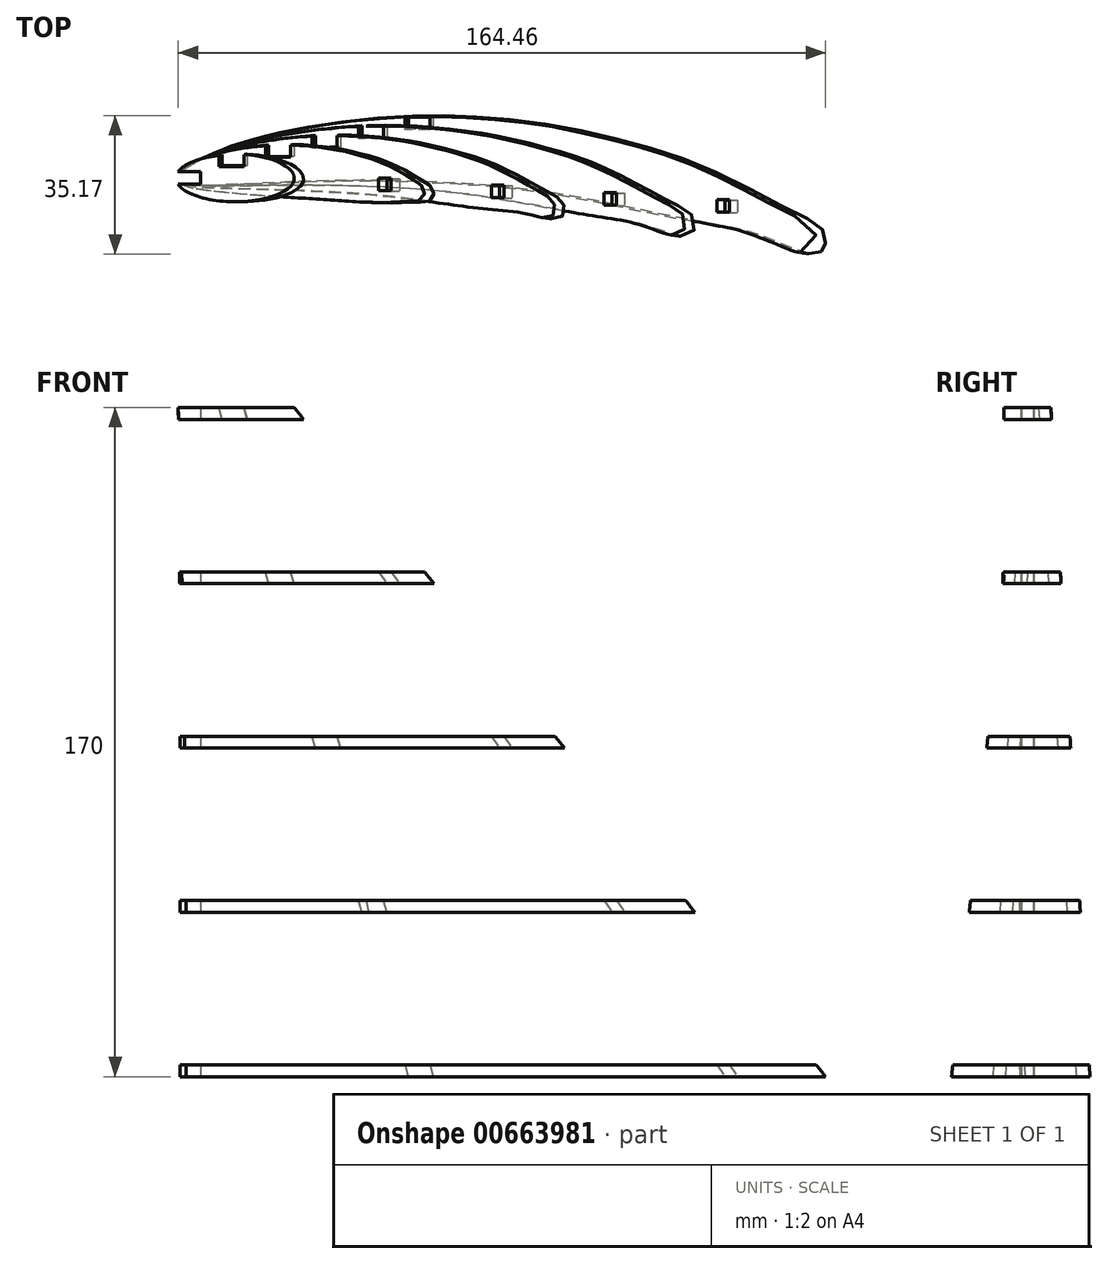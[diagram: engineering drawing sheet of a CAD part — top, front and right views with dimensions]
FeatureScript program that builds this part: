
annotation { "Feature Type Name" : "Feature", "Feature Type Description" : "" }
export const myFeature = defineFeature(function(context is Context, id is Id, definition is map)
    precondition{}
    {
        {
            var Q0;
            Q0=qCreatedBy(makeId("Top.planeOp"),FACE);
            var sketch = newSketch(context, id + "F0", { "sketchPlane" : qUnion([Q0])});
            skLineSegment(sketch, "E0", {"start": v(1, 1.71) * mm, "end": v(3.22, 2.99) * mm});
            skLineSegment(sketch, "E1", {"start": v(3.22, 2.99) * mm, "end": v(5.44, 4.24) * mm});
            skLineSegment(sketch, "E2", {"start": v(5.44, 4.24) * mm, "end": v(7.68, 5.43) * mm});
            skLineSegment(sketch, "E3", {"start": v(7.68, 5.43) * mm, "end": v(9.99, 6.53) * mm});
            skLineSegment(sketch, "E4", {"start": v(9.99, 6.53) * mm, "end": v(12.3, 7.5) * mm});
            skLineSegment(sketch, "E5", {"start": v(12.3, 7.5) * mm, "end": v(14.68, 8.38) * mm});
            skLineSegment(sketch, "E6", {"start": v(14.68, 8.38) * mm, "end": v(17.1, 9.17) * mm});
            skLineSegment(sketch, "E7", {"start": v(17.1, 9.17) * mm, "end": v(19.55, 9.87) * mm});
            skLineSegment(sketch, "E8", {"start": v(19.55, 9.87) * mm, "end": v(22.03, 10.5) * mm});
            skLineSegment(sketch, "E9", {"start": v(22.03, 10.5) * mm, "end": v(26.45, 11.52) * mm});
            skLineSegment(sketch, "E10", {"start": v(26.45, 11.52) * mm, "end": v(29.5, 12.16) * mm});
            skLineSegment(sketch, "E11", {"start": v(29.5, 12.16) * mm, "end": v(34.51, 13.11) * mm});
            skLineSegment(sketch, "E12", {"start": v(34.51, 13.11) * mm, "end": v(37.02, 13.54) * mm});
            skLineSegment(sketch, "E13", {"start": v(37.02, 13.54) * mm, "end": v(39.53, 13.94) * mm});
            skLineSegment(sketch, "E14", {"start": v(39.53, 13.94) * mm, "end": v(42.04, 14.3) * mm});
            skLineSegment(sketch, "E15", {"start": v(42.04, 14.3) * mm, "end": v(44.56, 14.62) * mm});
            skLineSegment(sketch, "E16", {"start": v(44.56, 14.62) * mm, "end": v(48.06, 15.01) * mm});
            skLineSegment(sketch, "E17", {"start": v(48.06, 15.01) * mm, "end": v(49.61, 15.16) * mm});
            skLineSegment(sketch, "E18", {"start": v(49.61, 15.16) * mm, "end": v(52.14, 15.37) * mm});
            skLineSegment(sketch, "E19", {"start": v(52.14, 15.37) * mm, "end": v(54.68, 15.53) * mm});
            skLineSegment(sketch, "E20", {"start": v(54.68, 15.53) * mm, "end": v(57.22, 15.66) * mm});
            skLineSegment(sketch, "E21", {"start": v(57.22, 15.66) * mm, "end": v(59.76, 15.76) * mm});
            skLineSegment(sketch, "E22", {"start": v(59.76, 15.76) * mm, "end": v(62.3, 15.81) * mm});
            skLineSegment(sketch, "E23", {"start": v(62.3, 15.81) * mm, "end": v(64.85, 15.83) * mm});
            skLineSegment(sketch, "E24", {"start": v(64.85, 15.83) * mm, "end": v(67.4, 15.82) * mm});
            skLineSegment(sketch, "E25", {"start": v(67.4, 15.82) * mm, "end": v(69.95, 15.77) * mm});
            skLineSegment(sketch, "E26", {"start": v(69.95, 15.77) * mm, "end": v(72.67, 15.68) * mm});
            skLineSegment(sketch, "E27", {"start": v(72.67, 15.68) * mm, "end": v(75.03, 15.57) * mm});
            skLineSegment(sketch, "E28", {"start": v(75.03, 15.57) * mm, "end": v(77.57, 15.42) * mm});
            skLineSegment(sketch, "E29", {"start": v(77.57, 15.42) * mm, "end": v(80.11, 15.23) * mm});
            skLineSegment(sketch, "E30", {"start": v(80.11, 15.23) * mm, "end": v(82.65, 15.02) * mm});
            skLineSegment(sketch, "E31", {"start": v(82.65, 15.02) * mm, "end": v(85.18, 14.77) * mm});
            skLineSegment(sketch, "E32", {"start": v(85.18, 14.77) * mm, "end": v(87.7, 14.49) * mm});
            skLineSegment(sketch, "E33", {"start": v(87.7, 14.49) * mm, "end": v(90.23, 14.17) * mm});
            skLineSegment(sketch, "E34", {"start": v(90.23, 14.17) * mm, "end": v(92.75, 13.82) * mm});
            skLineSegment(sketch, "E35", {"start": v(92.75, 13.82) * mm, "end": v(95.26, 13.44) * mm});
            skLineSegment(sketch, "E36", {"start": v(95.26, 13.44) * mm, "end": v(97.77, 13.02) * mm});
            skLineSegment(sketch, "E37", {"start": v(97.77, 13.02) * mm, "end": v(100.27, 12.56) * mm});
            skLineSegment(sketch, "E38", {"start": v(100.27, 12.56) * mm, "end": v(102.77, 12.08) * mm});
            skLineSegment(sketch, "E39", {"start": v(102.77, 12.08) * mm, "end": v(105.26, 11.56) * mm});
            skLineSegment(sketch, "E40", {"start": v(105.26, 11.56) * mm, "end": v(107.74, 11) * mm});
            skLineSegment(sketch, "E41", {"start": v(107.74, 11) * mm, "end": v(110.22, 10.41) * mm});
            skLineSegment(sketch, "E42", {"start": v(110.22, 10.41) * mm, "end": v(112.68, 9.79) * mm});
            skLineSegment(sketch, "E43", {"start": v(112.68, 9.79) * mm, "end": v(115.14, 9.13) * mm});
            skLineSegment(sketch, "E44", {"start": v(115.14, 9.13) * mm, "end": v(117.6, 8.44) * mm});
            skLineSegment(sketch, "E45", {"start": v(117.6, 8.44) * mm, "end": v(120.03, 7.72) * mm});
            skLineSegment(sketch, "E46", {"start": v(120.03, 7.72) * mm, "end": v(121.72, 7.2) * mm});
            skLineSegment(sketch, "E47", {"start": v(121.72, 7.2) * mm, "end": v(124.88, 6.17) * mm});
            skLineSegment(sketch, "E48", {"start": v(124.88, 6.17) * mm, "end": v(127.29, 5.34) * mm});
            skLineSegment(sketch, "E49", {"start": v(127.29, 5.34) * mm, "end": v(129.68, 4.48) * mm});
            skLineSegment(sketch, "E50", {"start": v(129.68, 4.48) * mm, "end": v(132.06, 3.58) * mm});
            skLineSegment(sketch, "E51", {"start": v(132.06, 3.58) * mm, "end": v(134.43, 2.64) * mm});
            skLineSegment(sketch, "E52", {"start": v(134.43, 2.64) * mm, "end": v(136.78, 1.66) * mm});
            skLineSegment(sketch, "E53", {"start": v(136.78, 1.66) * mm, "end": v(139.1, 0.64) * mm});
            skLineSegment(sketch, "E54", {"start": v(139.1, 0.64) * mm, "end": v(142.17, -0.78) * mm});
            skLineSegment(sketch, "E55", {"start": v(142.17, -0.78) * mm, "end": v(143.7, -1.53) * mm});
            skLineSegment(sketch, "E56", {"start": v(143.7, -1.53) * mm, "end": v(145.97, -2.68) * mm});
            skLineSegment(sketch, "E57", {"start": v(145.97, -2.68) * mm, "end": v(148.22, -3.85) * mm});
            skLineSegment(sketch, "E58", {"start": v(148.22, -3.85) * mm, "end": v(152.69, -6.28) * mm});
            skLineSegment(sketch, "E59", {"start": v(152.69, -6.28) * mm, "end": v(157.13, -8.76) * mm});
            skLineSegment(sketch, "E60", {"start": v(1, 1.71) * mm, "end": v(0.87, 1.54) * mm});
            skLineSegment(sketch, "E61", {"start": v(0.87, 1.54) * mm, "end": v(0.73, 1.38) * mm});
            skLineSegment(sketch, "E62", {"start": v(0.73, 1.38) * mm, "end": v(0.6, 1.21) * mm});
            skLineSegment(sketch, "E63", {"start": v(0.6, 1.21) * mm, "end": v(0.48, 1.05) * mm});
            skLineSegment(sketch, "E64", {"start": v(0.48, 1.05) * mm, "end": v(0.42, 0.97) * mm});
            skLineSegment(sketch, "E65", {"start": v(0.42, 0.97) * mm, "end": v(0.37, 0.9) * mm});
            skLineSegment(sketch, "E66", {"start": v(0.37, 0.9) * mm, "end": v(0.33, 0.84) * mm});
            skLineSegment(sketch, "E67", {"start": v(0.33, 0.84) * mm, "end": v(0.27, 0.74) * mm});
            skLineSegment(sketch, "E68", {"start": v(0.27, 0.74) * mm, "end": v(0.23, 0.67) * mm});
            skLineSegment(sketch, "E69", {"start": v(0.23, 0.67) * mm, "end": v(0.19, 0.6) * mm});
            skLineSegment(sketch, "E70", {"start": v(0.19, 0.6) * mm, "end": v(0.15, 0.52) * mm});
            skLineSegment(sketch, "E71", {"start": v(0.15, 0.52) * mm, "end": v(0.12, 0.45) * mm});
            skLineSegment(sketch, "E72", {"start": v(0.12, 0.45) * mm, "end": v(0.1, 0.38) * mm});
            skLineSegment(sketch, "E73", {"start": v(0.1, 0.38) * mm, "end": v(0.07, 0.32) * mm});
            skLineSegment(sketch, "E74", {"start": v(0.07, 0.32) * mm, "end": v(0.05, 0.25) * mm});
            skLineSegment(sketch, "E75", {"start": v(0.05, 0.25) * mm, "end": v(0.03, 0.19) * mm});
            skLineSegment(sketch, "E76", {"start": v(0.03, 0.19) * mm, "end": v(0.02, 0.12) * mm});
            skLineSegment(sketch, "E77", {"start": v(0.02, 0.12) * mm, "end": v(0, 0.06) * mm});
            skLineSegment(sketch, "E78", {"start": v(0, 0.06) * mm, "end": v(0, 0) * mm});
            skLineSegment(sketch, "E79", {"start": v(0, 0) * mm, "end": v(0, -0.06) * mm});
            skLineSegment(sketch, "E80", {"start": v(0, -0.06) * mm, "end": v(0, -0.12) * mm});
            skLineSegment(sketch, "E81", {"start": v(0, -0.12) * mm, "end": v(0, -0.18) * mm});
            skLineSegment(sketch, "E82", {"start": v(0, -0.18) * mm, "end": v(0, -0.23) * mm});
            skLineSegment(sketch, "E83", {"start": v(0, -0.23) * mm, "end": v(0.02, -0.29) * mm});
            skLineSegment(sketch, "E84", {"start": v(0.02, -0.29) * mm, "end": v(0.03, -0.34) * mm});
            skLineSegment(sketch, "E85", {"start": v(0.03, -0.34) * mm, "end": v(0.05, -0.4) * mm});
            skLineSegment(sketch, "E86", {"start": v(0.05, -0.4) * mm, "end": v(0.07, -0.44) * mm});
            skLineSegment(sketch, "E87", {"start": v(0.07, -0.44) * mm, "end": v(0.1, -0.5) * mm});
            skLineSegment(sketch, "E88", {"start": v(0.1, -0.5) * mm, "end": v(0.12, -0.54) * mm});
            skLineSegment(sketch, "E89", {"start": v(0.12, -0.54) * mm, "end": v(0.15, -0.6) * mm});
            skLineSegment(sketch, "E90", {"start": v(0.15, -0.6) * mm, "end": v(0.18, -0.64) * mm});
            skLineSegment(sketch, "E91", {"start": v(0.18, -0.64) * mm, "end": v(0.22, -0.68) * mm});
            skLineSegment(sketch, "E92", {"start": v(0.22, -0.68) * mm, "end": v(0.25, -0.73) * mm});
            skLineSegment(sketch, "E93", {"start": v(0.25, -0.73) * mm, "end": v(0.3, -0.77) * mm});
            skLineSegment(sketch, "E94", {"start": v(0.3, -0.77) * mm, "end": v(0.34, -0.81) * mm});
            skLineSegment(sketch, "E95", {"start": v(0.34, -0.81) * mm, "end": v(0.39, -0.86) * mm});
            skLineSegment(sketch, "E96", {"start": v(0.39, -0.86) * mm, "end": v(0.44, -0.9) * mm});
            skLineSegment(sketch, "E97", {"start": v(0.44, -0.9) * mm, "end": v(0.5, -0.94) * mm});
            skLineSegment(sketch, "E98", {"start": v(0.5, -0.94) * mm, "end": v(0.6, -1.01) * mm});
            skLineSegment(sketch, "E99", {"start": v(0.6, -1.01) * mm, "end": v(0.73, -1.08) * mm});
            skLineSegment(sketch, "E100", {"start": v(0.73, -1.08) * mm, "end": v(0.87, -1.15) * mm});
            skLineSegment(sketch, "E101", {"start": v(0.87, -1.15) * mm, "end": v(1.02, -1.22) * mm});
            skLineSegment(sketch, "E102", {"start": v(1.02, -1.22) * mm, "end": v(1.17, -1.28) * mm});
            skLineSegment(sketch, "E103", {"start": v(1.17, -1.28) * mm, "end": v(1.34, -1.33) * mm});
            skLineSegment(sketch, "E104", {"start": v(1.34, -1.33) * mm, "end": v(1.52, -1.39) * mm});
            skLineSegment(sketch, "E105", {"start": v(1.52, -1.39) * mm, "end": v(1.7, -1.44) * mm});
            skLineSegment(sketch, "E106", {"start": v(1.7, -1.44) * mm, "end": v(1.9, -1.48) * mm});
            skLineSegment(sketch, "E107", {"start": v(1.9, -1.48) * mm, "end": v(2.1, -1.53) * mm});
            skLineSegment(sketch, "E108", {"start": v(2.1, -1.53) * mm, "end": v(2.32, -1.57) * mm});
            skLineSegment(sketch, "E109", {"start": v(2.32, -1.57) * mm, "end": v(2.54, -1.6) * mm});
            skLineSegment(sketch, "E110", {"start": v(2.54, -1.6) * mm, "end": v(2.77, -1.64) * mm});
            skLineSegment(sketch, "E111", {"start": v(2.77, -1.64) * mm, "end": v(3, -1.67) * mm});
            skLineSegment(sketch, "E112", {"start": v(3, -1.67) * mm, "end": v(3.25, -1.7) * mm});
            skLineSegment(sketch, "E113", {"start": v(3.25, -1.7) * mm, "end": v(3.5, -1.73) * mm});
            skLineSegment(sketch, "E114", {"start": v(3.5, -1.73) * mm, "end": v(3.77, -1.75) * mm});
            skLineSegment(sketch, "E115", {"start": v(3.77, -1.75) * mm, "end": v(4.03, -1.77) * mm});
            skLineSegment(sketch, "E116", {"start": v(4.03, -1.77) * mm, "end": v(4.3, -1.8) * mm});
            skLineSegment(sketch, "E117", {"start": v(4.3, -1.8) * mm, "end": v(4.59, -1.8) * mm});
            skLineSegment(sketch, "E118", {"start": v(4.59, -1.8) * mm, "end": v(4.87, -1.82) * mm});
            skLineSegment(sketch, "E119", {"start": v(4.87, -1.82) * mm, "end": v(5.16, -1.83) * mm});
            skLineSegment(sketch, "E120", {"start": v(5.16, -1.83) * mm, "end": v(5.46, -1.84) * mm});
            skLineSegment(sketch, "E121", {"start": v(5.46, -1.84) * mm, "end": v(5.76, -1.85) * mm});
            skLineSegment(sketch, "E122", {"start": v(5.76, -1.85) * mm, "end": v(6.07, -1.86) * mm});
            skLineSegment(sketch, "E123", {"start": v(6.07, -1.86) * mm, "end": v(6.38, -1.86) * mm});
            skLineSegment(sketch, "E124", {"start": v(6.38, -1.86) * mm, "end": v(6.7, -1.87) * mm});
            skLineSegment(sketch, "E125", {"start": v(6.7, -1.87) * mm, "end": v(7.02, -1.87) * mm});
            skLineSegment(sketch, "E126", {"start": v(7.02, -1.87) * mm, "end": v(7.34, -1.87) * mm});
            skLineSegment(sketch, "E127", {"start": v(7.34, -1.87) * mm, "end": v(7.67, -1.87) * mm});
            skLineSegment(sketch, "E128", {"start": v(7.67, -1.87) * mm, "end": v(8, -1.87) * mm});
            skLineSegment(sketch, "E129", {"start": v(8, -1.87) * mm, "end": v(8.34, -1.86) * mm});
            skLineSegment(sketch, "E130", {"start": v(8.34, -1.86) * mm, "end": v(8.67, -1.86) * mm});
            skLineSegment(sketch, "E131", {"start": v(8.67, -1.86) * mm, "end": v(9.36, -1.85) * mm});
            skLineSegment(sketch, "E132", {"start": v(9.36, -1.85) * mm, "end": v(10.05, -1.83) * mm});
            skLineSegment(sketch, "E133", {"start": v(10.05, -1.83) * mm, "end": v(10.74, -1.82) * mm});
            skLineSegment(sketch, "E134", {"start": v(10.74, -1.82) * mm, "end": v(12.15, -1.78) * mm});
            skLineSegment(sketch, "E135", {"start": v(157.13, -8.76) * mm, "end": v(159.65, -9.9) * mm});
            skLineSegment(sketch, "E136", {"start": v(159.65, -9.9) * mm, "end": v(162.12, -11.02) * mm});
            skLineSegment(sketch, "E137", {"start": v(162.12, -11.02) * mm, "end": v(163.97, -12.8) * mm});
            skLineSegment(sketch, "E138", {"start": v(163.97, -12.8) * mm, "end": v(165.18, -13.97) * mm});
            skLineSegment(sketch, "E139", {"start": v(165.18, -13.97) * mm, "end": v(165.11, -15.41) * mm});
            skLineSegment(sketch, "E140", {"start": v(165.11, -15.41) * mm, "end": v(164.85, -16.72) * mm});
            skLineSegment(sketch, "E141", {"start": v(164.85, -16.72) * mm, "end": v(164.68, -17.32) * mm});
            skLineSegment(sketch, "E142", {"start": v(164.68, -17.32) * mm, "end": v(164.48, -17.86) * mm});
            skLineSegment(sketch, "E143", {"start": v(164.48, -17.86) * mm, "end": v(164.28, -18.24) * mm});
            skLineSegment(sketch, "E144", {"start": v(164.28, -18.24) * mm, "end": v(163.92, -18.7) * mm});
            skLineSegment(sketch, "E145", {"start": v(163.92, -18.7) * mm, "end": v(163.55, -18.98) * mm});
            skLineSegment(sketch, "E146", {"start": v(163.55, -18.98) * mm, "end": v(163.13, -19.18) * mm});
            skLineSegment(sketch, "E147", {"start": v(163.13, -19.18) * mm, "end": v(162.66, -19.3) * mm});
            skLineSegment(sketch, "E148", {"start": v(162.66, -19.3) * mm, "end": v(162.15, -19.36) * mm});
            skLineSegment(sketch, "E149", {"start": v(162.15, -19.36) * mm, "end": v(161.6, -19.35) * mm});
            skLineSegment(sketch, "E150", {"start": v(161.6, -19.35) * mm, "end": v(161, -19.28) * mm});
            skLineSegment(sketch, "E151", {"start": v(161, -19.28) * mm, "end": v(160.39, -19.16) * mm});
            skLineSegment(sketch, "E152", {"start": v(160.39, -19.16) * mm, "end": v(159.74, -19) * mm});
            skLineSegment(sketch, "E153", {"start": v(159.74, -19) * mm, "end": v(159.07, -18.79) * mm});
            skLineSegment(sketch, "E154", {"start": v(159.07, -18.79) * mm, "end": v(158.37, -18.54) * mm});
            skLineSegment(sketch, "E155", {"start": v(158.37, -18.54) * mm, "end": v(156.94, -17.98) * mm});
            skLineSegment(sketch, "E156", {"start": v(156.94, -17.98) * mm, "end": v(155.48, -17.36) * mm});
            skLineSegment(sketch, "E157", {"start": v(155.48, -17.36) * mm, "end": v(153.3, -16.41) * mm});
            skLineSegment(sketch, "E158", {"start": v(153.3, -16.41) * mm, "end": v(152.58, -16.1) * mm});
            skLineSegment(sketch, "E159", {"start": v(152.58, -16.1) * mm, "end": v(151.19, -15.54) * mm});
            skLineSegment(sketch, "E160", {"start": v(151.19, -15.54) * mm, "end": v(149.84, -15.03) * mm});
            skLineSegment(sketch, "E161", {"start": v(149.84, -15.03) * mm, "end": v(148.53, -14.57) * mm});
            skLineSegment(sketch, "E162", {"start": v(148.53, -14.57) * mm, "end": v(147.26, -14.14) * mm});
            skLineSegment(sketch, "E163", {"start": v(147.26, -14.14) * mm, "end": v(146.02, -13.76) * mm});
            skLineSegment(sketch, "E164", {"start": v(146.02, -13.76) * mm, "end": v(144.8, -13.4) * mm});
            skLineSegment(sketch, "E165", {"start": v(144.8, -13.4) * mm, "end": v(143.62, -13.09) * mm});
            skLineSegment(sketch, "E166", {"start": v(143.62, -13.09) * mm, "end": v(142.46, -12.8) * mm});
            skLineSegment(sketch, "E167", {"start": v(142.46, -12.8) * mm, "end": v(140.2, -12.3) * mm});
            skLineSegment(sketch, "E168", {"start": v(140.2, -12.3) * mm, "end": v(137.98, -11.85) * mm});
            skLineSegment(sketch, "E169", {"start": v(137.98, -11.85) * mm, "end": v(133.6, -11.09) * mm});
            skLineSegment(sketch, "E170", {"start": v(133.6, -11.09) * mm, "end": v(131.7, -10.76) * mm});
            skLineSegment(sketch, "E171", {"start": v(131.7, -10.76) * mm, "end": v(129.14, -10.3) * mm});
            skLineSegment(sketch, "E172", {"start": v(129.14, -10.3) * mm, "end": v(126.85, -9.85) * mm});
            skLineSegment(sketch, "E173", {"start": v(126.85, -9.85) * mm, "end": v(124.52, -9.39) * mm});
            skLineSegment(sketch, "E174", {"start": v(124.52, -9.39) * mm, "end": v(122.15, -8.9) * mm});
            skLineSegment(sketch, "E175", {"start": v(122.15, -8.9) * mm, "end": v(119.76, -8.4) * mm});
            skLineSegment(sketch, "E176", {"start": v(119.76, -8.4) * mm, "end": v(114.91, -7.38) * mm});
            skLineSegment(sketch, "E177", {"start": v(114.91, -7.38) * mm, "end": v(110, -6.37) * mm});
            skLineSegment(sketch, "E178", {"start": v(110, -6.37) * mm, "end": v(105.06, -5.4) * mm});
            skLineSegment(sketch, "E179", {"start": v(105.06, -5.4) * mm, "end": v(100.77, -4.6) * mm});
            skLineSegment(sketch, "E180", {"start": v(100.77, -4.6) * mm, "end": v(95.2, -3.7) * mm});
            skLineSegment(sketch, "E181", {"start": v(95.2, -3.7) * mm, "end": v(90.32, -3.02) * mm});
            skLineSegment(sketch, "E182", {"start": v(90.32, -3.02) * mm, "end": v(85.45, -2.43) * mm});
            skLineSegment(sketch, "E183", {"start": v(85.45, -2.43) * mm, "end": v(80.6, -1.94) * mm});
            skLineSegment(sketch, "E184", {"start": v(80.6, -1.94) * mm, "end": v(75.74, -1.53) * mm});
            skLineSegment(sketch, "E185", {"start": v(75.74, -1.53) * mm, "end": v(70.88, -1.2) * mm});
            skLineSegment(sketch, "E186", {"start": v(70.88, -1.2) * mm, "end": v(66.02, -0.95) * mm});
            skLineSegment(sketch, "E187", {"start": v(66.02, -0.95) * mm, "end": v(61.14, -0.76) * mm});
            skLineSegment(sketch, "E188", {"start": v(61.14, -0.76) * mm, "end": v(56.25, -0.64) * mm});
            skLineSegment(sketch, "E189", {"start": v(56.25, -0.64) * mm, "end": v(51.35, -0.58) * mm});
            skLineSegment(sketch, "E190", {"start": v(51.35, -0.58) * mm, "end": v(46.44, -0.58) * mm});
            skLineSegment(sketch, "E191", {"start": v(46.44, -0.58) * mm, "end": v(41.53, -0.63) * mm});
            skLineSegment(sketch, "E192", {"start": v(41.53, -0.63) * mm, "end": v(34.6, -0.78) * mm});
            skLineSegment(sketch, "E193", {"start": v(34.6, -0.78) * mm, "end": v(31.72, -0.88) * mm});
            skLineSegment(sketch, "E194", {"start": v(31.72, -0.88) * mm, "end": v(21.93, -1.29) * mm});
            skLineSegment(sketch, "E195", {"start": v(21.93, -1.29) * mm, "end": v(12.15, -1.78) * mm});
            skSolve(sketch);
        }
        {
            var Q0;
            Q0=qCreatedBy(makeId("Top.planeOp"),FACE);
            var sketch = newSketch(context, id + "F1", { "sketchPlane" : qUnion([Q0])});
            skPoint(sketch, "E196.0", {"position": v(0, 0) * mm});
            skPoint(sketch, "E196.1", {"position": v(0.1, 0.38) * mm});
            skPoint(sketch, "E196.2", {"position": v(0.33, 0.84) * mm});
            skPoint(sketch, "E196.3", {"position": v(0.73, 1.38) * mm});
            skPoint(sketch, "E196.4", {"position": v(5.44, 4.24) * mm});
            skPoint(sketch, "E196.5", {"position": v(12.3, 7.5) * mm});
            skPoint(sketch, "E196.6", {"position": v(22.03, 10.5) * mm});
            skPoint(sketch, "E196.7", {"position": v(57.22, 15.66) * mm});
            skPoint(sketch, "E196.8", {"position": v(75.03, 15.57) * mm});
            skPoint(sketch, "E196.9", {"position": v(95.26, 13.44) * mm});
            skPoint(sketch, "E196.10", {"position": v(117.6, 8.44) * mm});
            skPoint(sketch, "E196.11", {"position": v(136.78, 1.66) * mm});
            skPoint(sketch, "E196.12", {"position": v(157.13, -8.76) * mm});
            skPoint(sketch, "E196.13", {"position": v(163.97, -12.8) * mm});
            skPoint(sketch, "E196.14", {"position": v(164.48, -17.86) * mm});
            skPoint(sketch, "E196.15", {"position": v(163.55, -18.98) * mm});
            skPoint(sketch, "E196.16", {"position": v(160.39, -19.16) * mm});
            skPoint(sketch, "E196.17", {"position": v(155.48, -17.36) * mm});
            skPoint(sketch, "E196.18", {"position": v(148.53, -14.57) * mm});
            skPoint(sketch, "E196.19", {"position": v(143.62, -13.09) * mm});
            skPoint(sketch, "E196.20", {"position": v(105.06, -5.4) * mm});
            skPoint(sketch, "E196.21", {"position": v(80.6, -1.94) * mm});
            skPoint(sketch, "E196.22", {"position": v(51.35, -0.58) * mm});
            skPoint(sketch, "E196.23", {"position": v(21.93, -1.29) * mm});
            skPoint(sketch, "E196.24", {"position": v(9.36, -1.85) * mm});
            skPoint(sketch, "E196.25", {"position": v(5.46, -1.84) * mm});
            skPoint(sketch, "E196.26", {"position": v(3, -1.67) * mm});
            skPoint(sketch, "E196.27", {"position": v(0.39, -0.86) * mm});
            skPoint(sketch, "E196.28", {"position": v(0.1, -0.5) * mm});
            skPoint(sketch, "E196.29", {"position": v(35.77, 13.33) * mm});
            skPoint(sketch, "E196.30", {"position": v(164.98, -16.07) * mm});
            skPoint(sketch, "E196.31", {"position": v(125.68, -9.62) * mm});
            skPoint(sketch, "E196.32", {"position": v(38.06, -0.7) * mm});
            skFitSpline(sketch, "E197", {"points": [v(0, 0) * mm, v(0.1, 0.38) * mm, v(0.33, 0.84) * mm, v(0.73, 1.38) * mm, v(5.44, 4.24) * mm, v(12.3, 7.5) * mm, v(22.03, 10.5) * mm, v(35.77, 13.33) * mm, v(57.22, 15.66) * mm, v(75.03, 15.57) * mm, v(95.26, 13.44) * mm, v(117.6, 8.44) * mm, v(136.78, 1.66) * mm, v(157.13, -8.76) * mm, v(163.97, -12.8) * mm, v(164.98, -16.07) * mm, v(164.48, -17.86) * mm, v(163.55, -18.98) * mm, v(160.39, -19.16) * mm, v(155.48, -17.36) * mm, v(148.53, -14.57) * mm, v(143.62, -13.09) * mm, v(125.68, -9.62) * mm, v(105.06, -5.4) * mm, v(80.6, -1.94) * mm, v(51.35, -0.58) * mm, v(38.06, -0.7) * mm, v(21.93, -1.29) * mm, v(9.36, -1.85) * mm, v(5.46, -1.84) * mm, v(3, -1.67) * mm, v(0.39, -0.86) * mm, v(0.1, -0.5) * mm, v(0, 0) * mm]});
            skSolve(sketch);
        }
        {
            var Q0;
            Q0=qCreatedBy(makeId("Top.planeOp"),FACE);
            cPlane(context, id + "F2", {"entities" : qUnion([Q0]), "cplaneType" : CPlaneType.OFFSET, "offset" : 170 * mm, "width" : 150 * mm, "height" : 150 * mm});
        }
        {
            var Q0;
            Q0=qCreatedBy(id+"F2.planeOp",FACE);
            var sketch = newSketch(context, id + "F3", { "sketchPlane" : qUnion([Q0])});
            skEllipse(sketch, "E198", {"center": v(15, 0) * mm, "majorRadius": 15 * mm, "minorRadius": 6.01 * mm, "majorAxis": v(-1, 0)});
            skSolve(sketch);
        }
        {
            var Q0;
            Q0=makeQuery(id+"F1.imprint","IMPRINT",FACE,{"disambiguationData":[TD([[makeQuery(id+"F1.imprint","IMPRINT",EDGE,{"derivedFrom":sQuery(id+"F1.wireOp",EDGE,"E197")}),-1.0]])]});
            var Q1;
            Q1=makeQuery(id+"F3.imprint","IMPRINT",FACE,{"disambiguationData":[TD([[makeQuery(id+"F3.imprint","IMPRINT",EDGE,{"derivedFrom":sQuery(id+"F3.wireOp",EDGE,"E198")}),1.0]])]});
            loft(context, id + "F4", {"sheetProfilesArray" : [{ "sheetProfileEntities" : qUnion([Q0]) }, { "sheetProfileEntities" : qUnion([Q1]) }]});
        }
        {
            var Q0;
            Q0=qCreatedBy(makeId("Front.planeOp"),FACE);
            var sketch = newSketch(context, id + "F5", { "sketchPlane" : qUnion([Q0])});
            skLineSegment(sketch, "E199", {"start": v(0, 0) * mm, "end": v(0, 3) * mm, "construction": true});
            skLineSegment(sketch, "E200.bottom", {"start": v(0, 3) * mm, "end": v(214.07, 3) * mm});
            skLineSegment(sketch, "E200.top", {"start": v(0, 41.75) * mm, "end": v(214.07, 41.75) * mm});
            skLineSegment(sketch, "E200.left", {"start": v(0, 3) * mm, "end": v(0, 41.75) * mm});
            skLineSegment(sketch, "E200.right", {"start": v(214.07, 3) * mm, "end": v(214.07, 41.75) * mm});
            skLineSegment(sketch, "E201", {"start": v(0, 41.75) * mm, "end": v(0, 44.75) * mm, "construction": true});
            skLineSegment(sketch, "E202.0.1.0", {"start": v(0, 83.5) * mm, "end": v(214.07, 83.5) * mm});
            skLineSegment(sketch, "E202.0.1.1", {"start": v(0, 44.75) * mm, "end": v(0, 83.5) * mm});
            skLineSegment(sketch, "E202.0.1.2", {"start": v(214.07, 44.75) * mm, "end": v(214.07, 83.5) * mm});
            skLineSegment(sketch, "E202.0.1.3", {"start": v(0, 44.75) * mm, "end": v(214.07, 44.75) * mm});
            skLineSegment(sketch, "E202.0.1.4", {"start": v(0, 83.5) * mm, "end": v(0, 86.5) * mm, "construction": true});
            skLineSegment(sketch, "E202.0.2.0", {"start": v(0, 125.25) * mm, "end": v(214.07, 125.25) * mm});
            skLineSegment(sketch, "E202.0.2.1", {"start": v(0, 86.5) * mm, "end": v(0, 125.25) * mm});
            skLineSegment(sketch, "E202.0.2.2", {"start": v(214.07, 86.5) * mm, "end": v(214.07, 125.25) * mm});
            skLineSegment(sketch, "E202.0.2.3", {"start": v(0, 86.5) * mm, "end": v(214.07, 86.5) * mm});
            skLineSegment(sketch, "E202.0.2.4", {"start": v(0, 125.25) * mm, "end": v(0, 128.25) * mm, "construction": true});
            skLineSegment(sketch, "E202.0.2.5", {"start": v(0, 83.5) * mm, "end": v(0, 86.5) * mm, "construction": true});
            skLineSegment(sketch, "E202.0.3.0", {"start": v(0, 167) * mm, "end": v(214.07, 167) * mm});
            skLineSegment(sketch, "E202.0.3.1", {"start": v(0, 128.25) * mm, "end": v(0, 167) * mm});
            skLineSegment(sketch, "E202.0.3.2", {"start": v(214.07, 128.25) * mm, "end": v(214.07, 167) * mm});
            skLineSegment(sketch, "E202.0.3.3", {"start": v(0, 128.25) * mm, "end": v(214.07, 128.25) * mm});
            skLineSegment(sketch, "E202.0.3.4", {"start": v(0, 167) * mm, "end": v(0, 170) * mm, "construction": true});
            skLineSegment(sketch, "E202.0.3.5", {"start": v(0, 125.25) * mm, "end": v(0, 128.25) * mm, "construction": true});
            skLineSegment(sketch, "E202.direction1", {"start": v(0, 0) * mm, "end": v(25, 0) * mm, "construction": true});
            skLineSegment(sketch, "E202.direction2", {"start": v(0, 0) * mm, "end": v(0, 41.75) * mm, "construction": true});
            skSolve(sketch);
        }
        {
            var Q0;
            Q0=qSketchRegion(id+"F5",true);
            extrude(context, id + "F6", {"entities" : qUnion([Q0]), "operationType" : NewBodyOperationType.REMOVE, "oppositeDirection" : true, "depth" : 25 * mm, "offsetDistance" : 25 * mm});
        }
        {
            var Q0;
            Q0=qSketchRegion(id+"F5",true);
            extrude(context, id + "F7", {"entities" : qUnion([Q0]), "operationType" : NewBodyOperationType.REMOVE, "depth" : 25 * mm, "offsetDistance" : 25 * mm});
        }
        {
            var Q0;
            Q0=qCreatedBy(makeId("Top.planeOp"),FACE);
            var sketch = newSketch(context, id + "F8", { "sketchPlane" : qUnion([Q0])});
            skLineSegment(sketch, "E203", {"start": v(0, 0) * mm, "end": v(3, 0) * mm, "construction": true});
            skLineSegment(sketch, "E204.bottom", {"start": v(6.17, -1.59) * mm, "end": v(-0.17, -1.59) * mm});
            skLineSegment(sketch, "E204.top", {"start": v(6.17, 1.59) * mm, "end": v(-0.17, 1.59) * mm});
            skLineSegment(sketch, "E204.left", {"start": v(6.17, -1.59) * mm, "end": v(6.17, 1.59) * mm});
            skLineSegment(sketch, "E204.right", {"start": v(-0.17, -1.59) * mm, "end": v(-0.18, 1.59) * mm});
            skPoint(sketch, "E204.middle", {"position": v(3, 0) * mm});
            skSolve(sketch);
        }
        {
            var Q0;
            Q0=makeQuery(id+"F8.imprint","IMPRINT",FACE,{"disambiguationData":[TD([[makeQuery(id+"F8.imprint","IMPRINT",EDGE,{"derivedFrom":sQuery(id+"F8.wireOp",EDGE,"E204.bottom")}),-1.0]])]});
            extrude(context, id + "F9", {"entities" : qUnion([Q0]), "operationType" : NewBodyOperationType.REMOVE, "depth" : 204.2 * mm, "offsetDistance" : 25 * mm});
        }
        {
            var Q0;
            Q0=qCreatedBy(makeId("Top.planeOp"),FACE);
            var sketch = newSketch(context, id + "F10", { "sketchPlane" : qUnion([Q0])});
            skPoint(sketch, "E205", {"position": v(62.22, 15.71) * mm});
            skLineSegment(sketch, "E206", {"start": v(62.22, 15.71) * mm, "end": v(62.22, 12.5) * mm, "construction": true});
            skLineSegment(sketch, "E207", {"start": v(62.22, 12.5) * mm, "end": v(59.05, 12.5) * mm});
            skLineSegment(sketch, "E208", {"start": v(62.22, 12.5) * mm, "end": v(65.4, 12.5) * mm});
            skLineSegment(sketch, "E209", {"start": v(65.4, 12.5) * mm, "end": v(65.4, 15.71) * mm});
            skLineSegment(sketch, "E210", {"start": v(65.4, 15.71) * mm, "end": v(59.05, 15.71) * mm});
            skLineSegment(sketch, "E211", {"start": v(59.05, 15.71) * mm, "end": v(59.05, 12.5) * mm});
            skPoint(sketch, "E212", {"position": v(14.04, 6.12) * mm});
            skLineSegment(sketch, "E213", {"start": v(14.04, 6.12) * mm, "end": v(14.04, 2.95) * mm, "construction": true});
            skLineSegment(sketch, "E214", {"start": v(14.04, 2.95) * mm, "end": v(10.86, 2.95) * mm});
            skLineSegment(sketch, "E215", {"start": v(10.86, 2.95) * mm, "end": v(10.86, 6.12) * mm});
            skLineSegment(sketch, "E216", {"start": v(10.86, 6.12) * mm, "end": v(14.04, 6.12) * mm});
            skLineSegment(sketch, "E217", {"start": v(14.04, 6.12) * mm, "end": v(17.22, 6.12) * mm});
            skLineSegment(sketch, "E218", {"start": v(17.22, 6.12) * mm, "end": v(17.22, 2.95) * mm});
            skLineSegment(sketch, "E219", {"start": v(17.22, 2.95) * mm, "end": v(14.04, 2.95) * mm});
            skSolve(sketch);
        }
        {
            var Q0;
            Q0=makeQuery(id+"F4.opLoft","CAP_FACE",FACE,{"disambiguationData":[OSD([makeQuery(id+"F3.imprint","IMPRINT",FACE,{"disambiguationData":[TD([[makeQuery(id+"F3.imprint","IMPRINT",EDGE,{"derivedFrom":sQuery(id+"F3.wireOp",EDGE,"E198")}),1.0]])]})])],"isStart":true});
            var sketch = newSketch(context, id + "F11", { "sketchPlane" : qUnion([Q0])});
            skLineSegment(sketch, "E220", {"start": v(17.27, 2.94) * mm, "end": v(10.85, 2.94) * mm});
            skLineSegment(sketch, "E221", {"start": v(10.85, 2.94) * mm, "end": v(10.85, 6.1) * mm});
            skLineSegment(sketch, "E222", {"start": v(10.85, 6.1) * mm, "end": v(17.23, 6.1) * mm});
            skLineSegment(sketch, "E223", {"start": v(17.23, 6.1) * mm, "end": v(17.27, 2.94) * mm});
            skSolve(sketch);
        }
        {
            var Q0;
            Q0=sQuery(id+"F11.wireOp",VERTEX,"E221.start");
            var Q1;
            Q1=sQuery(id+"F10.wireOp",VERTEX,"E211.start");
            var Q2;
            Q2=sQuery(id+"F10.wireOp",VERTEX,"E211.end");
            cPlane(context, id + "F12", {"entities" : qUnion([Q0, Q1, Q2]), "cplaneType" : CPlaneType.THREE_POINT, "offset" : 25 * mm, "width" : 150 * mm, "height" : 150 * mm});
        }
        {
            var Q0;
            Q0=qCreatedBy(id+"F12.planeOp",FACE);
            var sketch = newSketch(context, id + "F13", { "sketchPlane" : qUnion([Q0])});
            skPoint(sketch, "E224.0", {"position": v(2.94, 160.6) * mm});
            skPoint(sketch, "E225.0", {"position": v(12.5, -16.1) * mm});
            skLineSegment(sketch, "E226", {"start": v(12.5, -16.1) * mm, "end": v(2.94, 160.6) * mm});
            skSolve(sketch);
        }
        {
            var Q0;
            Q0=makeQuery(id+"F10.imprint","IMPRINT",FACE,{"disambiguationData":[TD([[makeQuery(id+"F10.imprint","IMPRINT",EDGE,{"derivedFrom":sQuery(id+"F10.wireOp",EDGE,"E207")}),-1.0]])]});
            var Q1;
            Q1=sQuery(id+"F13.wireOp",EDGE,"E226");
            sweep(context, id + "F14", {"operationType" : NewBodyOperationType.REMOVE, "profiles" : qUnion([Q0]), "path" : qUnion([Q1])});
        }
        {
            var Q0;
            {var subQ0=sQuery(id+"F5.wireOp",EDGE,"E202.0.3.3");Q0=makeQuery(id+"F7.boolean.opBoolean","MERGE",FACE,{"derivedFrom":[makeQuery(id+"F6.boolean.opBoolean","COPY",FACE,{"derivedFrom":makeQuery(id+"F6.opExtrude","SWEPT_FACE",FACE,{"disambiguationData":[OSD([subQ0])]})}),makeQuery(id+"F7.opExtrude","SWEPT_FACE",FACE,{"disambiguationData":[OSD([subQ0])]})]});}
            var sketch = newSketch(context, id + "F15", { "sketchPlane" : qUnion([Q0])});
            skLineSegment(sketch, "E227.bottom", {"start": v(51.47, 0) * mm, "end": v(54.64, 0) * mm});
            skLineSegment(sketch, "E227.top", {"start": v(51.47, -3.18) * mm, "end": v(54.64, -3.18) * mm});
            skLineSegment(sketch, "E227.left", {"start": v(51.47, 0) * mm, "end": v(51.47, -3.18) * mm});
            skLineSegment(sketch, "E227.right", {"start": v(54.64, 0) * mm, "end": v(54.64, -3.18) * mm});
            skSolve(sketch);
        }
        {
            var Q0;
            Q0=makeQuery(id+"F4.opLoft","CAP_FACE",FACE,{"disambiguationData":[OSD([makeQuery(id+"F1.imprint","IMPRINT",FACE,{"disambiguationData":[TD([[makeQuery(id+"F1.imprint","IMPRINT",EDGE,{"derivedFrom":sQuery(id+"F1.wireOp",EDGE,"E197")}),-1.0]])]})])],"isStart":true});
            var sketch = newSketch(context, id + "F16", { "sketchPlane" : qUnion([Q0])});
            skLineSegment(sketch, "E228.bottom", {"start": v(139.4, 5.64) * mm, "end": v(142.58, 5.64) * mm});
            skLineSegment(sketch, "E228.top", {"start": v(139.4, 8.82) * mm, "end": v(142.58, 8.82) * mm});
            skLineSegment(sketch, "E228.left", {"start": v(139.4, 5.64) * mm, "end": v(139.4, 8.82) * mm});
            skLineSegment(sketch, "E228.right", {"start": v(142.58, 5.64) * mm, "end": v(142.58, 8.82) * mm});
            skPoint(sketch, "E228.middle", {"position": v(141, 7.23) * mm});
            skSolve(sketch);
        }
        {
            var Q0;
            Q0=qSketchRegion(id+"F15",true);
            var Q1;
            Q1=qSketchRegion(id+"F16",true);
            loft(context, id + "F17", {"operationType" : NewBodyOperationType.REMOVE, "sheetProfilesArray" : [{ "sheetProfileEntities" : qUnion([Q0]) }, { "sheetProfileEntities" : qUnion([Q1]) }]});
        }
    });
